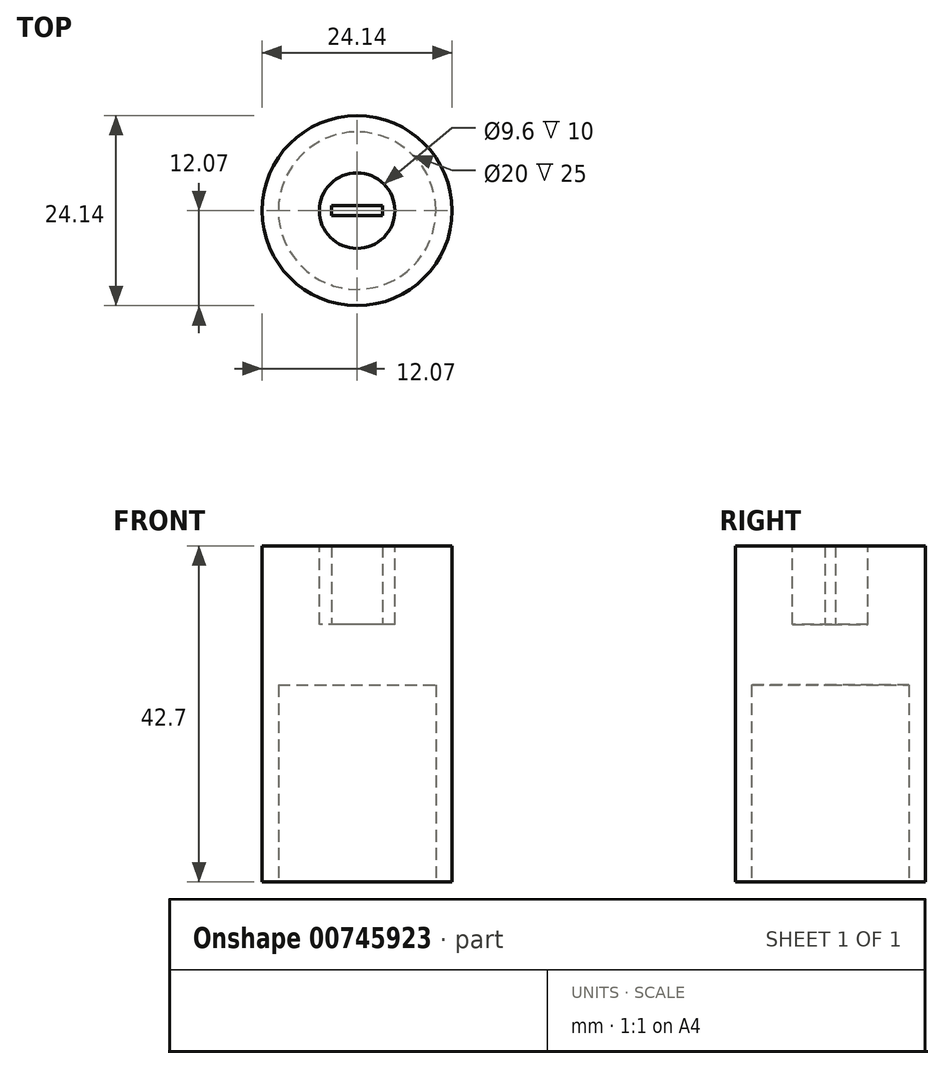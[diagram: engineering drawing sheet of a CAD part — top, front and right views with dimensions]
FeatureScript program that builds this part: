
annotation { "Feature Type Name" : "Feature", "Feature Type Description" : "" }
export const myFeature = defineFeature(function(context is Context, id is Id, definition is map)
    precondition{}
    {
        {
            var Q0;
            Q0=qCreatedBy(makeId("Top.planeOp"),FACE);
            var sketch = newSketch(context, id + "F0", { "sketchPlane" : qUnion([Q0])});
            skCircle(sketch, "E0", {"center": v(0, 0) * mm, "radius": 12.07 * mm});
            skSolve(sketch);
        }
        {
            var Q0;
            Q0 = qSketchRegion(id + "F0", true);
            var Q1;
            Q1=makeQuery(id+"F0.imprint","IMPRINT",FACE,{"disambiguationData":[TD([[makeQuery(id+"F0.imprint","IMPRINT",EDGE,{"derivedFrom":sQuery(id+"F0.wireOp",EDGE,"E0")}),1.0]])]});
            extrude(context, id + "F1", {"entities" : qUnion([Q0, Q1]), "depth" : 42.7 * mm, "offsetDistance" : 25 * mm});
        }
        {
            var Q0;
            Q0=makeQuery(id+"F1.opExtrude","CAP_FACE",FACE,{"disambiguationData":[OSD([sQuery(id+"F0.wireOp",EDGE,"E0")])],"isStart":false});
            var sketch = newSketch(context, id + "F2", { "sketchPlane" : qUnion([Q0])});
            skCircle(sketch, "E1", {"center": v(0, 0) * mm, "radius": 4.8 * mm});
            skSolve(sketch);
        }
        {
            var Q0;
            Q0=makeQuery(id+"F2.imprint","IMPRINT",FACE,{"disambiguationData":[TD([[makeQuery(id+"F2.imprint","IMPRINT",EDGE,{"derivedFrom":sQuery(id+"F2.wireOp",EDGE,"E1")}),1.0]])]});
            extrude(context, id + "F3", {"entities" : qUnion([Q0]), "operationType" : NewBodyOperationType.REMOVE, "oppositeDirection" : true, "depth" : 10 * mm, "offsetDistance" : 25 * mm});
        }
        {
            var Q0;
            Q0=makeQuery(id+"F3.boolean.opBoolean","COPY",FACE,{"derivedFrom":makeQuery(id+"F3.opExtrude","CAP_FACE",FACE,{"disambiguationData":[OSD([sQuery(id+"F2.wireOp",EDGE,"E1")])],"isStart":false})});
            var sketch = newSketch(context, id + "F4", { "sketchPlane" : qUnion([Q0])});
            skLineSegment(sketch, "E2.bottom", {"start": v(3.25, -0.65) * mm, "end": v(-3.25, -0.65) * mm});
            skLineSegment(sketch, "E2.top", {"start": v(3.25, 0.65) * mm, "end": v(-3.25, 0.65) * mm});
            skLineSegment(sketch, "E2.left", {"start": v(3.25, -0.65) * mm, "end": v(3.25, 0.65) * mm});
            skLineSegment(sketch, "E2.right", {"start": v(-3.25, -0.65) * mm, "end": v(-3.25, 0.65) * mm});
            skPoint(sketch, "E2.middle", {"position": v(0, 0) * mm});
            skSolve(sketch);
        }
        {
            var Q0;
            Q0=makeQuery(id+"F4.imprint","IMPRINT",FACE,{"disambiguationData":[TD([[makeQuery(id+"F4.imprint","IMPRINT",EDGE,{"derivedFrom":sQuery(id+"F4.wireOp",EDGE,"E2.bottom")}),-1.0]])]});
            extrude(context, id + "F5", {"entities" : qUnion([Q0]), "operationType" : NewBodyOperationType.ADD, "depth" : 10 * mm, "offsetDistance" : 25 * mm});
        }
        {
            var Q0;
            Q0=makeQuery(id+"F1.opExtrude","CAP_FACE",FACE,{"disambiguationData":[OSD([sQuery(id+"F0.wireOp",EDGE,"E0")])],"isStart":true});
            var sketch = newSketch(context, id + "F6", { "sketchPlane" : qUnion([Q0])});
            skCircle(sketch, "E3", {"center": v(0, 0) * mm, "radius": 10 * mm});
            skSolve(sketch);
        }
        {
            var Q0;
            Q0=makeQuery(id+"F6.imprint","IMPRINT",FACE,{"disambiguationData":[TD([[makeQuery(id+"F6.imprint","IMPRINT",EDGE,{"derivedFrom":sQuery(id+"F6.wireOp",EDGE,"E3")}),1.0]])]});
            extrude(context, id + "F7", {"entities" : qUnion([Q0]), "operationType" : NewBodyOperationType.REMOVE, "oppositeDirection" : true, "depth" : 25 * mm, "offsetDistance" : 25 * mm});
        }
    });
